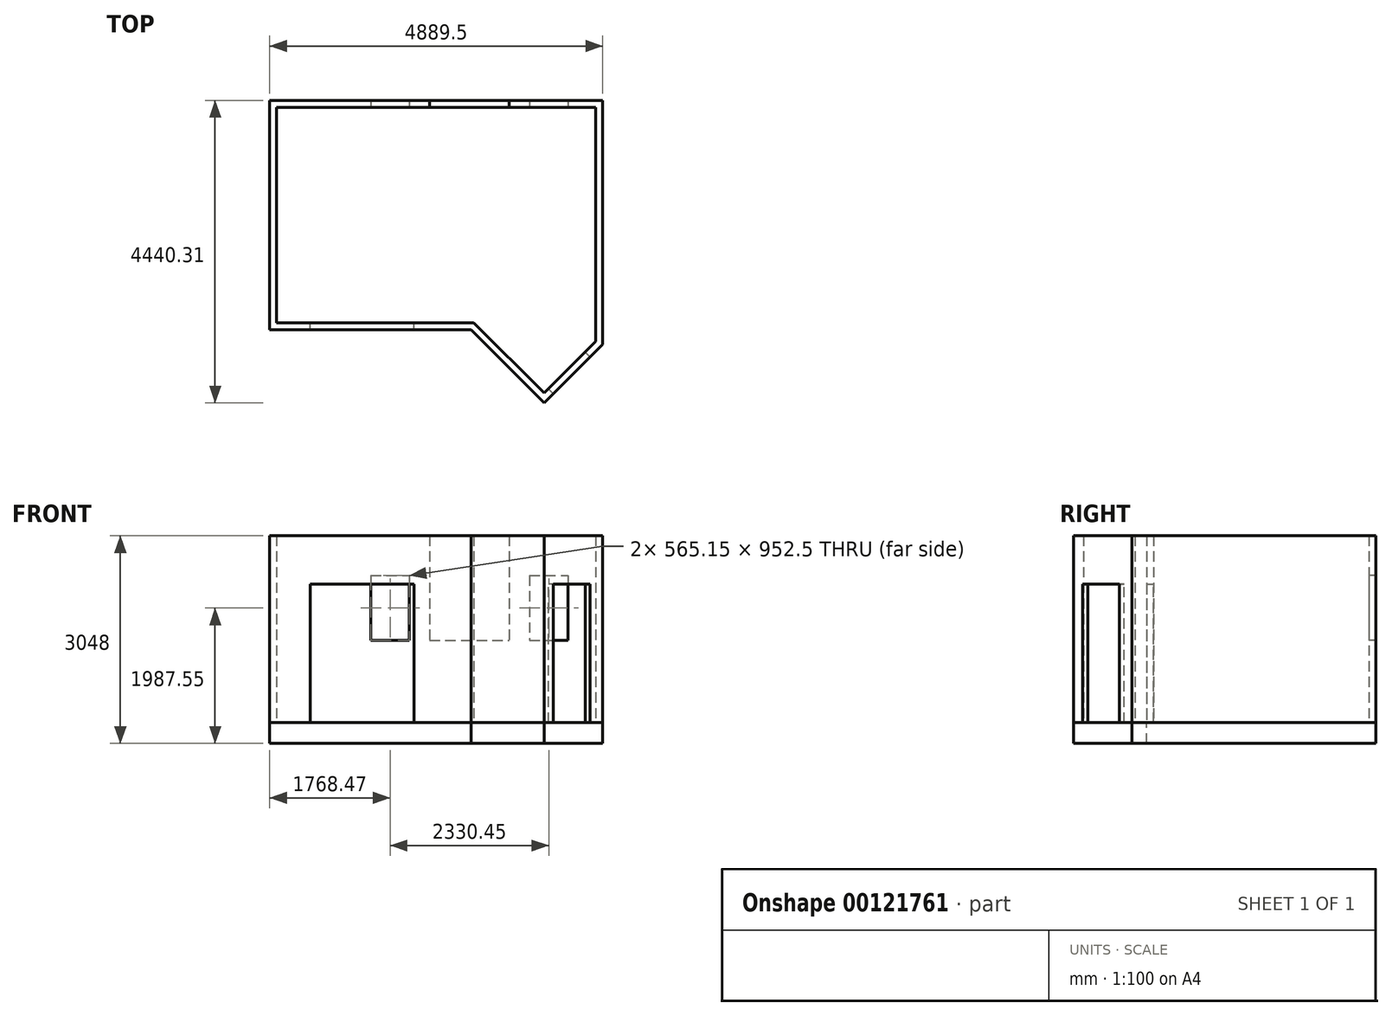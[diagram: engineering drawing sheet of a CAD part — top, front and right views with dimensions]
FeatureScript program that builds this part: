
annotation { "Feature Type Name" : "Feature", "Feature Type Description" : "" }
export const myFeature = defineFeature(function(context is Context, id is Id, definition is map)
    precondition{}
    {
        {
            var Q0;
            Q0=qCreatedBy(makeId("Top.planeOp"),FACE);
            var sketch = newSketch(context, id + "F0", { "sketchPlane" : qUnion([Q0])});
            skLineSegment(sketch, "E0.bottom", {"start": v(0, 0) * mm, "end": v(-4686.3, 0) * mm});
            skLineSegment(sketch, "E0.top", {"start": v(-1790.7, -3162.3) * mm, "end": v(-4686.3, -3162.3) * mm});
            skLineSegment(sketch, "E0.left", {"start": v(0, 0) * mm, "end": v(0, -3437.06) * mm});
            skLineSegment(sketch, "E0.right", {"start": v(-4686.3, 0) * mm, "end": v(-4686.3, -3162.3) * mm});
            skLineSegment(sketch, "E1.0", {"start": v(-4787.9, 101.6) * mm, "end": v(-4787.9, -3263.9) * mm});
            skLineSegment(sketch, "E2.0", {"start": v(101.6, 101.6) * mm, "end": v(-4787.9, 101.6) * mm});
            skLineSegment(sketch, "E3.0", {"start": v(101.6, 101.6) * mm, "end": v(101.6, -3479.14) * mm});
            skLineSegment(sketch, "E4", {"start": v(-1790.7, -3162.3) * mm, "end": v(-757.97, -4195.03) * mm});
            skLineSegment(sketch, "E5", {"start": v(-757.97, -4195.03) * mm, "end": v(0, -3437.06) * mm});
            skLineSegment(sketch, "E6.0", {"start": v(-1832.78, -3263.9) * mm, "end": v(-757.97, -4338.71) * mm});
            skLineSegment(sketch, "E7.0", {"start": v(-757.97, -4338.71) * mm, "end": v(101.6, -3479.14) * mm});
            skLineSegment(sketch, "E8.trimOffspring", {"start": v(-1832.78, -3263.9) * mm, "end": v(-4787.9, -3263.9) * mm});
            skSolve(sketch);
        }
        {
            var Q0;
            Q0=makeQuery(id+"F0.imprint","IMPRINT",FACE,{"disambiguationData":[TD([[makeQuery(id+"F0.imprint","IMPRINT",EDGE,{"derivedFrom":sQuery(id+"F0.wireOp",EDGE,"E0.bottom")}),-1.0]])]});
            extrude(context, id + "F1", {"entities" : qUnion([Q0]), "depth" : 2743.2 * mm});
        }
        {
            var Q0;
            Q0=qCreatedBy(makeId("Top.planeOp"),FACE);
            var sketch = newSketch(context, id + "F2", { "sketchPlane" : qUnion([Q0])});
            skLineSegment(sketch, "E9.0", {"start": v(101.6, 101.6) * mm, "end": v(101.6, -3479.14) * mm});
            skLineSegment(sketch, "E10.0", {"start": v(-757.97, -4338.71) * mm, "end": v(101.6, -3479.14) * mm});
            skLineSegment(sketch, "E11.0", {"start": v(-1832.78, -3263.9) * mm, "end": v(-757.97, -4338.71) * mm});
            skLineSegment(sketch, "E12.0", {"start": v(-1832.78, -3263.9) * mm, "end": v(-4787.9, -3263.9) * mm});
            skLineSegment(sketch, "E13.0", {"start": v(-4787.9, 101.6) * mm, "end": v(-4787.9, -3263.9) * mm});
            skLineSegment(sketch, "E14.0", {"start": v(101.6, 101.6) * mm, "end": v(-4787.9, 101.6) * mm});
            skSolve(sketch);
        }
        {
            var Q0;
            Q0=makeQuery(id+"F2.imprint","IMPRINT",FACE,{"disambiguationData":[TD([[makeQuery(id+"F2.imprint","IMPRINT",EDGE,{"derivedFrom":sQuery(id+"F2.wireOp",EDGE,"E9.0")}),-1.0]])]});
            extrude(context, id + "F3", {"entities" : qUnion([Q0]), "oppositeDirection" : true, "depth" : 304.8 * mm});
        }
        {
            var Q0;
            Q0=makeQuery(id+"F1.opExtrude","SWEPT_FACE",FACE,{"disambiguationData":[OSD([sQuery(id+"F0.wireOp",EDGE,"E5")])]});
            var sketch = newSketch(context, id + "F4", { "sketchPlane" : qUnion([Q0])});
            skLineSegment(sketch, "E15.bottom", {"start": v(2651.4, 0) * mm, "end": v(3413.4, 0) * mm});
            skLineSegment(sketch, "E15.top", {"start": v(2651.4, 2032) * mm, "end": v(3413.4, 2032) * mm});
            skLineSegment(sketch, "E15.left", {"start": v(2651.4, 0) * mm, "end": v(2651.4, 2032) * mm});
            skLineSegment(sketch, "E15.right", {"start": v(3413.4, 0) * mm, "end": v(3413.4, 2032) * mm});
            skSolve(sketch);
        }
        {
            var Q0;
            Q0=makeQuery(id+"F4.imprint","IMPRINT",FACE,{"disambiguationData":[TD([[makeQuery(id+"F4.imprint","IMPRINT",EDGE,{"derivedFrom":sQuery(id+"F4.wireOp",EDGE,"E15.bottom")}),-1.0]])]});
            extrude(context, id + "F5", {"entities" : qUnion([Q0]), "operationType" : NewBodyOperationType.REMOVE, "endBound" : BoundingType.THROUGH_ALL, "oppositeDirection" : true, "depth" : 25.4 * mm});
        }
        {
            var Q0;
            Q0=makeQuery(id+"F1.opExtrude","SWEPT_FACE",FACE,{"disambiguationData":[OSD([sQuery(id+"F0.wireOp",EDGE,"E0.top")])]});
            var sketch = newSketch(context, id + "F6", { "sketchPlane" : qUnion([Q0])});
            skLineSegment(sketch, "E16.bottom", {"start": v(2667, 0) * mm, "end": v(4191, 0) * mm});
            skLineSegment(sketch, "E16.top", {"start": v(2667, 2032) * mm, "end": v(4191, 2032) * mm});
            skLineSegment(sketch, "E16.left", {"start": v(2667, 0) * mm, "end": v(2667, 2032) * mm});
            skLineSegment(sketch, "E16.right", {"start": v(4191, 0) * mm, "end": v(4191, 2032) * mm});
            skSolve(sketch);
        }
        {
            var Q0;
            Q0=makeQuery(id+"F6.imprint","IMPRINT",FACE,{"disambiguationData":[TD([[makeQuery(id+"F6.imprint","IMPRINT",EDGE,{"derivedFrom":sQuery(id+"F6.wireOp",EDGE,"E16.bottom")}),1.0]])]});
            extrude(context, id + "F7", {"entities" : qUnion([Q0]), "operationType" : NewBodyOperationType.REMOVE, "endBound" : BoundingType.THROUGH_ALL, "oppositeDirection" : true, "depth" : 25.4 * mm});
        }
        {
            var Q0;
            Q0=makeQuery(id+"F1.opExtrude","SWEPT_FACE",FACE,{"disambiguationData":[OSD([sQuery(id+"F0.wireOp",EDGE,"E0.bottom")])]});
            var sketch = newSketch(context, id + "F8", { "sketchPlane" : qUnion([Q0])});
            skLineSegment(sketch, "E17.bottom", {"start": v(-3302, 2159) * mm, "end": v(-2736.85, 2159) * mm});
            skLineSegment(sketch, "E17.top", {"start": v(-3302, 1206.5) * mm, "end": v(-2736.85, 1206.5) * mm});
            skLineSegment(sketch, "E17.left", {"start": v(-3302, 2159) * mm, "end": v(-3302, 1206.5) * mm});
            skLineSegment(sketch, "E17.right", {"start": v(-2736.85, 2159) * mm, "end": v(-2736.85, 1206.5) * mm});
            skLineSegment(sketch, "E18.bottom", {"start": v(-2438.4, 2743.2) * mm, "end": v(-1270, 2743.2) * mm});
            skLineSegment(sketch, "E18.top", {"start": v(-2438.4, 1206.5) * mm, "end": v(-1270, 1206.5) * mm});
            skLineSegment(sketch, "E18.left", {"start": v(-2438.4, 2743.2) * mm, "end": v(-2438.4, 1206.5) * mm});
            skLineSegment(sketch, "E18.right", {"start": v(-1270, 2743.2) * mm, "end": v(-1270, 1206.5) * mm});
            skLineSegment(sketch, "E19.bottom", {"start": v(-971.55, 2159) * mm, "end": v(-406.4, 2159) * mm});
            skLineSegment(sketch, "E19.top", {"start": v(-971.55, 1206.5) * mm, "end": v(-406.4, 1206.5) * mm});
            skLineSegment(sketch, "E19.left", {"start": v(-971.55, 2159) * mm, "end": v(-971.55, 1206.5) * mm});
            skLineSegment(sketch, "E19.right", {"start": v(-406.4, 2159) * mm, "end": v(-406.4, 1206.5) * mm});
            skSolve(sketch);
        }
        {
            var Q0;
            Q0 = qSketchRegion(id + "F8", true);
            extrude(context, id + "F9", {"entities" : qUnion([Q0]), "operationType" : NewBodyOperationType.REMOVE, "endBound" : BoundingType.THROUGH_ALL, "oppositeDirection" : true, "depth" : 25.4 * mm});
        }
    });
